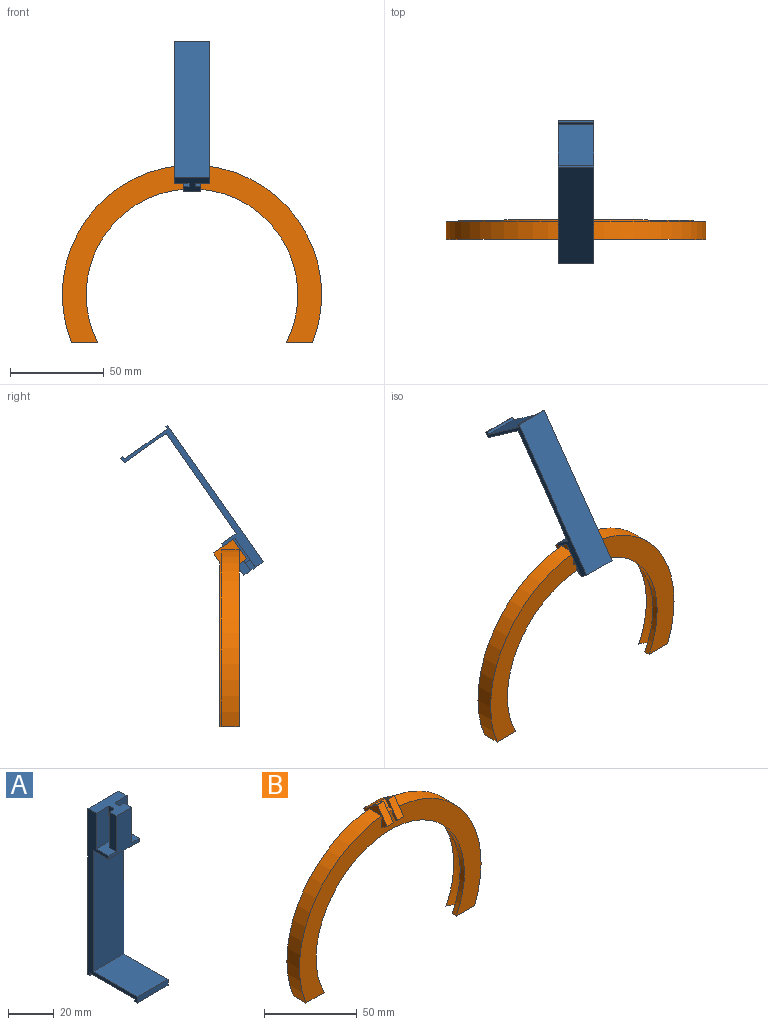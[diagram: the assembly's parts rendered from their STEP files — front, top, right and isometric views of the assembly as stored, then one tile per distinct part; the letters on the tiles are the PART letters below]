
ASSEMBLY  parts=2 mates=1
PART A: 32 faces, bbox 19.1x30.5x88.9 mm
  f0: plane 19.05x1.14mm, normal (0,0,-1), area 21.8mm2, adj f1,f2,f9,f30
  f1: plane 88.9x30.48mm, normal (-1,0,0), area 377.8mm2, adj f0,f6,f7,f8,f9,f10,f14,f25
  f2: plane 88.9x30.48mm, normal (1,0,0), area 379.1mm2, adj f0,f6,f7,f8,f9,f15,f16,f25
  f3: plane 13.97x3.2mm, normal (-1,0,0), area 44.7mm2, adj f10,f12,f14,f24
  f4: plane 13.97x3.14mm, normal (1,0,0), area 43.8mm2, adj f5,f15,f16,f20
  f5: plane 19.05x3.05mm, normal (0,1,0), area 58mm2, adj f4,f6,f15,f17,f18,f19,f20,f21
  f6: plane 19.05x12.7mm, normal (0,0,1), area 149.7mm2, adj f1,f2,f5,f7,f9,f11,f12,f13
  f7: plane 20.69x19.05mm, normal (0,-1,0), area 212.8mm2, adj f1,f2,f6,f10,f13,f15,f18,f26
  f8: plane 19.05x1.4mm, normal (0,0,-1), area 26.6mm2, adj f1,f2,f28,f29
  f9: plane 88.9x19.05mm, normal (0,1,0), area 1693.5mm2, adj f0,f1,f2,f6
  f10: plane 7.94x7.65mm, normal (0,0,1), area 46.6mm2, adj f1,f3,f7,f12,f13,f14
  f11: plane 4.85x3.2mm, normal (-1,0,0), area 15.5mm2, adj f6,f12,f14,f23
  f12: plane 19.05x3.18mm, normal (0,1,0), area 60.4mm2, adj f3,f6,f10,f11,f13,f22,f23,f24
  f13: plane 19.05x4.45mm, normal (-1,0,0), area 84.7mm2, adj f6,f7,f10,f12
  f14: plane 19.05x7.94mm, normal (0,-1,0), area 151.2mm2, adj f1,f3,f6,f10,f11,f22,f23,f24
  f15: plane 7.81x7.58mm, normal (0,0,1), area 45.7mm2, adj f2,f4,f5,f7,f16,f18
  f16: plane 19.05x7.81mm, normal (0,-1,0), area 148.8mm2, adj f2,f4,f6,f15,f17,f19,f20,f21
  f17: plane 4.85x3.14mm, normal (1,0,0), area 15.2mm2, adj f5,f6,f16,f21
  f18: plane 19.05x4.45mm, normal (1,0,0), area 84.7mm2, adj f5,f6,f7,f15
  f19: plane 3.14x0.23mm, normal (1,0,0), area 0.7mm2, adj f5,f16,f20,f21
  f20: plane 3.14x0.19mm, normal (0,0,-1), area 0.6mm2, adj f4,f5,f16,f19
  f21: plane 3.14x0.19mm, normal (0,0,1), area 0.6mm2, adj f5,f16,f17,f19
  f22: plane 3.2x0.23mm, normal (-1,0,0), area 0.7mm2, adj f12,f14,f23,f24
  f23: plane 3.2x0.19mm, normal (0,0,1), area 0.6mm2, adj f11,f12,f14,f22
  f24: plane 3.2x0.19mm, normal (0,0,-1), area 0.6mm2, adj f3,f12,f14,f22
  f25: plane 65.03x19.05mm, normal (0,-1,0), area 1238.8mm2, adj f1,f2,f26,f27
  f26: plane 19.05x9.53mm, normal (0,0,-1), area 181.5mm2, adj f1,f2,f7,f25
  f27: plane 27.31x19.05mm, normal (0,0,1), area 520.2mm2, adj f1,f2,f25,f28
  f28: plane 19.05x3.18mm, normal (0,-1,0), area 60.5mm2, adj f1,f2,f8,f27
  f29: plane 19.05x1.52mm, normal (0,1,0), area 29mm2, adj f1,f2,f8,f31
  f30: plane 19.05x1.52mm, normal (0,-1,0), area 29mm2, adj f0,f1,f2,f31
  f31: plane 27.94x19.05mm, normal (0,0,-1), area 532.3mm2, adj f1,f2,f29,f30
PART B: 33 faces, bbox 138.2x17.7x105.5 mm
  f0: plane 4.7x3.95mm, normal (0,-0.57,-0.82), area 13.4mm2, adj f2,f8,f18,f19,f20,f30
  f1: plane 4.32x3.2mm, normal (0,0.82,-0.57), area 16.3mm2, adj f11,f19,f21,f29
  f2: plane 5.09x2.39mm, normal (-1,0,0), area 6.1mm2, adj f0,f20,f30
  f3: plane 5.09x2.39mm, normal (1,0,0), area 6.1mm2, adj f17,f24,f30
  f4: plane 4.32x3.2mm, normal (0,0.82,-0.57), area 16.3mm2, adj f11,f23,f25,f29
  f5: revolved ~130.02x96.09mm, area 2548mm2, adj f13,f14,f21,f22,f23,f28,f31
  f6: plane 94.36x62.75mm, normal (0,1,0), area 783.8mm2, adj f9,f12,f13,f26
  f7: plane 12.7x4.93mm, normal (0,0.82,-0.57), area 76.4mm2, adj f8,f9,f11,f28
  f8: plane 17.69x13.17mm, normal (1,0,0), area 66mm2, adj f0,f7,f11,f15,f16,f18,f27,f28
  f9: plane 17.69x13.17mm, normal (-1,0,0), area 66mm2, adj f6,f7,f10,f11,f12,f17,f26,f28
  f10: plane 10.4x7.28mm, normal (0,-0.82,0.57), area 59.7mm2, adj f9,f11,f17,f25
  f11: plane 12.7x10.4mm, normal (0,0.57,0.82), area 112.1mm2, adj f1,f4,f7,f8,f9,f10,f18,f19
  f12: cylinder r=69.09mm len=94.36mm, axis (0,-1,0), area 1222.6mm2, adj f6,f9,f13,f30
  f13: plane 13.92x10.29mm, normal (0,0,-1), area 84.3mm2, adj f5,f6,f12,f26,f28,f30,f31,f32
  f14: plane 13.92x10.29mm, normal (0,0,-1), area 84.3mm2, adj f5,f15,f16,f27,f28,f30,f31,f32
  f15: cylinder r=69.09mm len=94.35mm, axis (0,-1,0), area 1222.4mm2, adj f8,f14,f16,f30
  f16: plane 94.35x62.73mm, normal (0,1,0), area 783.7mm2, adj f8,f14,f15,f27
  f17: plane 4.7x3.95mm, normal (0,-0.57,-0.82), area 13.4mm2, adj f3,f9,f10,f24,f25,f30
  f18: plane 10.4x7.28mm, normal (0,-0.82,0.57), area 59.7mm2, adj f0,f8,f11,f19
  f19: plane 11.5x8.85mm, normal (-1,0,0), area 21.4mm2, adj f0,f1,f11,f18,f20,f29,f30
  f20: plane 3.41x3.18mm, normal (0,0.82,-0.57), area 13.2mm2, adj f0,f2,f19,f30
  f21: plane 8.61x6.66mm, normal (-1,0,0), area 27.5mm2, adj f1,f5,f11,f22,f29,f31
  f22: plane 9.65x6.05mm, normal (0,-0.82,0.57), area 70.1mm2, adj f5,f11,f21,f23
  f23: plane 8.61x6.67mm, normal (1,0,0), area 27.5mm2, adj f4,f5,f11,f22,f29,f31
  f24: plane 3.41x3.18mm, normal (0,0.82,-0.57), area 13.2mm2, adj f3,f17,f25,f30
  f25: plane 11.5x8.85mm, normal (1,0,0), area 21.4mm2, adj f4,f10,f11,f17,f24,f29,f30
  f26: cylinder r=62.74mm len=87.98mm, axis (0,-1,0), area 90.3mm2, adj f6,f9,f13,f28
  f27: cylinder r=62.74mm len=87.97mm, axis (0,-1,0), area 90.3mm2, adj f8,f14,f16,f28
  f28: plane 125.48x87.98mm, normal (0,1,0), area 1013.3mm2, adj f5,f7,f8,f9,f13,f14,f26,f27
  f29: cylinder r=69.09mm len=9.65mm, axis (0,1,0), area 18.6mm2, adj f1,f4,f19,f21,f23,f25,f30,f31
  f30: plane 138.18x94.65mm, normal (0,-1,0), area 3130.8mm2, adj f0,f2,f3,f8,f9,f12,f13,f14
  f31: plane 130.04x94.65mm, normal (0,1,0), area 2140.6mm2, adj f5,f13,f14,f21,f23,f29,f32
  f32: cylinder r=56.39mm len=112.78mm, axis (0,1,0), area 736.7mm2, adj f13,f14,f30,f31
PLACE A rot(axis=(1,0,0),145deg) t=(9.53,34.97,135.09)mm
PLACE B at identity
MATE parallel A.f7 <-> B.f22  axis (0,0.82,-0.57) through (0.01,0.72,64.03)mm
